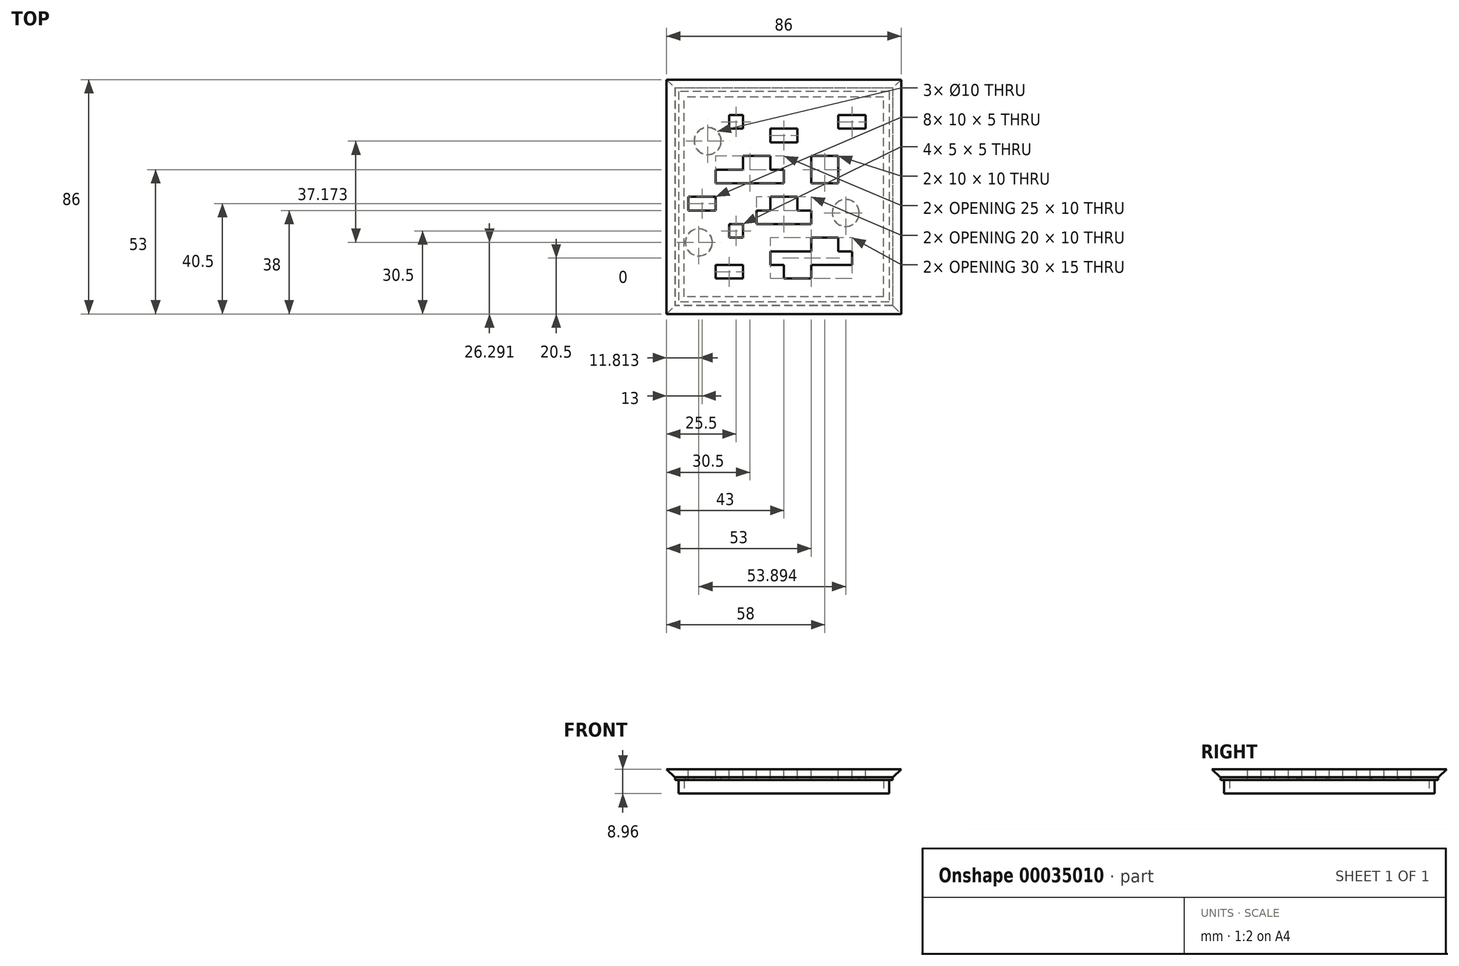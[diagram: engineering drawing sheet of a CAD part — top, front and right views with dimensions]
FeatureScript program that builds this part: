
annotation { "Feature Type Name" : "Feature", "Feature Type Description" : "" }
export const myFeature = defineFeature(function(context is Context, id is Id, definition is map)
    precondition{}
    {
        {
            var Q0;
            Q0=qCreatedBy(makeId("Top.planeOp"),FACE);
            var sketch = newSketch(context, id + "F0", { "sketchPlane" : qUnion([Q0])});
            skLineSegment(sketch, "E0.bottom", {"start": v(38.73, 38.72) * mm, "end": v(-38.72, 38.73) * mm});
            skLineSegment(sketch, "E0.top", {"start": v(38.72, -38.73) * mm, "end": v(-38.73, -38.72) * mm});
            skLineSegment(sketch, "E0.left", {"start": v(38.73, 38.72) * mm, "end": v(38.72, -38.73) * mm});
            skLineSegment(sketch, "E0.right", {"start": v(-38.72, 38.73) * mm, "end": v(-38.73, -38.72) * mm});
            skPoint(sketch, "E0.middle", {"position": v(0, 0) * mm});
            skLineSegment(sketch, "E1.0", {"start": v(38.62, 38.62) * mm, "end": v(-38.62, 38.62) * mm});
            skLineSegment(sketch, "E1.1", {"start": v(38.62, 38.62) * mm, "end": v(38.62, -38.63) * mm});
            skLineSegment(sketch, "E1.2", {"start": v(38.62, -38.63) * mm, "end": v(-38.62, -38.62) * mm});
            skLineSegment(sketch, "E1.3", {"start": v(-38.62, 38.62) * mm, "end": v(-38.62, -38.62) * mm});
            skLineSegment(sketch, "E2.bottom", {"start": v(36.62, -36.62) * mm, "end": v(-36.62, -36.62) * mm});
            skLineSegment(sketch, "E2.top", {"start": v(36.62, 36.62) * mm, "end": v(-36.62, 36.62) * mm});
            skLineSegment(sketch, "E2.left", {"start": v(36.62, -36.62) * mm, "end": v(36.62, 36.62) * mm});
            skLineSegment(sketch, "E2.right", {"start": v(-36.62, -36.62) * mm, "end": v(-36.62, 36.62) * mm});
            skSolve(sketch);
        }
        {
            var Q0;
            Q0=makeQuery(id+"F0.imprint","IMPRINT",FACE,{"disambiguationData":[TD([[makeQuery(id+"F0.imprint","IMPRINT",EDGE,{"derivedFrom":sQuery(id+"F0.wireOp",EDGE,"E1.0")}),1.0]])]});
            extrude(context, id + "F1", {"entities" : qUnion([Q0]), "depth" : 5 * mm});
        }
        {
            var Q0;
            Q0=makeQuery(id+"F1.opExtrude","CAP_FACE",FACE,{"disambiguationData":[OSD([sQuery(id+"F0.wireOp",EDGE,"E1.0"),sQuery(id+"F0.wireOp",EDGE,"E1.1"),sQuery(id+"F0.wireOp",EDGE,"E1.2"),sQuery(id+"F0.wireOp",EDGE,"E1.3")])],"isStart":false});
            var sketch = newSketch(context, id + "F2", { "sketchPlane" : qUnion([Q0])});
            skLineSegment(sketch, "E3.bottom", {"start": v(40, 40) * mm, "end": v(-40, 40) * mm});
            skLineSegment(sketch, "E3.top", {"start": v(40, -40) * mm, "end": v(-40, -40) * mm});
            skLineSegment(sketch, "E3.left", {"start": v(40, 40) * mm, "end": v(40, -40) * mm});
            skLineSegment(sketch, "E3.right", {"start": v(-40, 40) * mm, "end": v(-40, -40) * mm});
            skPoint(sketch, "E3.middle", {"position": v(0, 0) * mm});
            skLineSegment(sketch, "E4.0", {"start": v(39.9, 39.9) * mm, "end": v(39.9, -39.9) * mm});
            skLineSegment(sketch, "E4.1", {"start": v(39.9, 39.9) * mm, "end": v(-39.9, 39.9) * mm});
            skLineSegment(sketch, "E4.2", {"start": v(-39.9, 39.9) * mm, "end": v(-39.9, -39.9) * mm});
            skLineSegment(sketch, "E4.3", {"start": v(39.9, -39.9) * mm, "end": v(-39.9, -39.9) * mm});
            skSolve(sketch);
        }
        {
            var Q0;
            Q0=makeQuery(id+"F2.imprint","IMPRINT",FACE,{"disambiguationData":[TD([[makeQuery(id+"F2.imprint","IMPRINT",EDGE,{"derivedFrom":sQuery(id+"F2.wireOp",EDGE,"E4.0")}),-1.0]])]});
            var Q1;
            Q1=makeQuery(id+"F2.imprint","IMPRINT",FACE,{"disambiguationData":[TD([[makeQuery(id+"F2.imprint","IMPRINT",EDGE,{"derivedFrom":makeQuery(id+"F1.opExtrude","CAP_EDGE",EDGE,{"disambiguationData":[OSD([sQuery(id+"F0.wireOp",EDGE,"E1.0")])],"isStart":false})}),1.0]])]});
            var Q2;
            Q2=makeQuery(id+"F2.imprint","IMPRINT",FACE,{"disambiguationData":[TD([[makeQuery(id+"F2.imprint","IMPRINT",EDGE,{"derivedFrom":makeQuery(id+"F1.opExtrude","CAP_EDGE",EDGE,{"disambiguationData":[OSD([sQuery(id+"F0.wireOp",EDGE,"E2.bottom")])],"isStart":false})}),-1.0]])]});
            extrude(context, id + "F3", {"entities" : qUnion([Q0, Q1, Q2]), "operationType" : NewBodyOperationType.ADD, "depth" : 0.96 * mm});
        }
        {
            var Q0;
            Q0=makeQuery(id+"F3.opExtrude","CAP_FACE",FACE,{"disambiguationData":[OSD([sQuery(id+"F2.wireOp",EDGE,"E4.0"),sQuery(id+"F2.wireOp",EDGE,"E4.1"),sQuery(id+"F2.wireOp",EDGE,"E4.2"),sQuery(id+"F2.wireOp",EDGE,"E4.3")])],"isStart":false});
            var sketch = newSketch(context, id + "F4", { "sketchPlane" : qUnion([Q0])});
            skLineSegment(sketch, "E5.bottom", {"start": v(-34.9, -34.9) * mm, "end": v(34.9, -34.9) * mm, "construction": true});
            skLineSegment(sketch, "E5.top", {"start": v(-34.9, 34.9) * mm, "end": v(34.9, 34.9) * mm, "construction": true});
            skLineSegment(sketch, "E5.left", {"start": v(-34.9, -34.9) * mm, "end": v(-34.9, 34.9) * mm, "construction": true});
            skLineSegment(sketch, "E5.right", {"start": v(34.9, -34.9) * mm, "end": v(34.9, 34.9) * mm, "construction": true});
            skPoint(sketch, "E5.middle", {"position": v(0, 0) * mm});
            skCircle(sketch, "E6", {"center": v(-31.19, -16.7) * mm, "radius": 5 * mm});
            skCircle(sketch, "E7", {"center": v(22.7, -5.92) * mm, "radius": 5 * mm});
            skCircle(sketch, "E8", {"center": v(-27.93, 20.46) * mm, "radius": 5 * mm});
            skSolve(sketch);
        }
        {
            var Q0;
            Q0=makeQuery(id+"F4.imprint","IMPRINT",FACE,{"disambiguationData":[TD([[makeQuery(id+"F4.imprint","IMPRINT",EDGE,{"derivedFrom":sQuery(id+"F4.wireOp",EDGE,"E6")}),1.0]])]});
            var Q1;
            Q1=makeQuery(id+"F4.imprint","IMPRINT",FACE,{"disambiguationData":[TD([[makeQuery(id+"F4.imprint","IMPRINT",EDGE,{"derivedFrom":sQuery(id+"F4.wireOp",EDGE,"E8")}),1.0]])]});
            var Q2;
            Q2=makeQuery(id+"F4.imprint","IMPRINT",FACE,{"disambiguationData":[TD([[makeQuery(id+"F4.imprint","IMPRINT",EDGE,{"derivedFrom":sQuery(id+"F4.wireOp",EDGE,"E7")}),1.0]])]});
            var Q3;
            Q3=makeQuery(id+"F1.opExtrude","CAP_FACE",FACE,{"disambiguationData":[OSD([sQuery(id+"F0.wireOp",EDGE,"E1.0"),sQuery(id+"F0.wireOp",EDGE,"E1.1"),sQuery(id+"F0.wireOp",EDGE,"E1.2"),sQuery(id+"F0.wireOp",EDGE,"E1.3"),sQuery(id+"F0.wireOp",EDGE,"E2.bottom"),sQuery(id+"F0.wireOp",EDGE,"E2.top"),sQuery(id+"F0.wireOp",EDGE,"E2.left"),sQuery(id+"F0.wireOp",EDGE,"E2.right")])],"isStart":true});
            extrude(context, id + "F5", {"entities" : qUnion([Q0, Q1, Q2]), "operationType" : NewBodyOperationType.REMOVE, "endBound" : BoundingType.UP_TO_SURFACE, "oppositeDirection" : true, "endBoundEntityFace" : qUnion([Q3]), "depth" : 25 * mm});
        }
        {
            var Q0;
            Q0=makeQuery(id+"F3.opExtrude","CAP_FACE",FACE,{"disambiguationData":[OSD([sQuery(id+"F2.wireOp",EDGE,"E4.0"),sQuery(id+"F2.wireOp",EDGE,"E4.1"),sQuery(id+"F2.wireOp",EDGE,"E4.2"),sQuery(id+"F2.wireOp",EDGE,"E4.3")])],"isStart":false});
            var sketch = newSketch(context, id + "F6", { "sketchPlane" : qUnion([Q0])});
            skLineSegment(sketch, "E9.bottom", {"start": v(43, 43) * mm, "end": v(-43, 43) * mm});
            skLineSegment(sketch, "E9.top", {"start": v(43, -43) * mm, "end": v(-43, -43) * mm});
            skLineSegment(sketch, "E9.left", {"start": v(43, 43) * mm, "end": v(43, -43) * mm});
            skLineSegment(sketch, "E9.right", {"start": v(-43, 43) * mm, "end": v(-43, -43) * mm});
            skPoint(sketch, "E9.middle", {"position": v(0, 0) * mm});
            skSolve(sketch);
        }
        {
            var Q0;
            Q0 = qSketchRegion(id + "F6", true);
            extrude(context, id + "F7", {"entities" : qUnion([Q0]), "depth" : 3 * mm});
        }
        {
            var Q0;
            Q0=makeQuery(id+"F4.imprint","IMPRINT",FACE,{"disambiguationData":[TD([[makeQuery(id+"F4.imprint","IMPRINT",EDGE,{"derivedFrom":sQuery(id+"F4.wireOp",EDGE,"E6")}),-1.0]])]});
            var sketch = newSketch(context, id + "F8", { "sketchPlane" : qUnion([Q0])});
            skPoint(sketch, "E10.0", {"position": v(-31.19, -16.7) * mm});
            skCircle(sketch, "E11", {"center": v(-31.19, -16.7) * mm, "radius": 4.9 * mm});
            skPoint(sketch, "E12.0", {"position": v(22.7, -5.92) * mm});
            skPoint(sketch, "E13.0", {"position": v(-27.93, 20.46) * mm});
            skCircle(sketch, "E14", {"center": v(-27.93, 20.46) * mm, "radius": 4.9 * mm});
            skCircle(sketch, "E15", {"center": v(22.7, -5.92) * mm, "radius": 4.9 * mm});
            skSolve(sketch);
        }
        {
            var Q0;
            Q0=makeQuery(id+"F8.imprint","IMPRINT",FACE,{"disambiguationData":[TD([[makeQuery(id+"F8.imprint","IMPRINT",EDGE,{"derivedFrom":sQuery(id+"F8.wireOp",EDGE,"E11")}),1.0]])]});
            var Q1;
            Q1=makeQuery(id+"F8.imprint","IMPRINT",FACE,{"disambiguationData":[TD([[makeQuery(id+"F8.imprint","IMPRINT",EDGE,{"derivedFrom":sQuery(id+"F8.wireOp",EDGE,"E15")}),1.0]])]});
            var Q2;
            Q2=makeQuery(id+"F8.imprint","IMPRINT",FACE,{"disambiguationData":[TD([[makeQuery(id+"F8.imprint","IMPRINT",EDGE,{"derivedFrom":sQuery(id+"F8.wireOp",EDGE,"E14")}),1.0]])]});
            extrude(context, id + "F9", {"entities" : qUnion([Q0, Q1, Q2]), "operationType" : NewBodyOperationType.ADD, "oppositeDirection" : true, "depth" : 1 * mm});
        }
        {
            var Q0;
            Q0=makeQuery(id+"F7.opExtrude","CAP_FACE",FACE,{"disambiguationData":[OSD([sQuery(id+"F6.wireOp",EDGE,"E9.bottom"),sQuery(id+"F6.wireOp",EDGE,"E9.top"),sQuery(id+"F6.wireOp",EDGE,"E9.left"),sQuery(id+"F6.wireOp",EDGE,"E9.right")])],"isStart":false});
            var sketch = newSketch(context, id + "F10", { "sketchPlane" : qUnion([Q0])});
            skLineSegment(sketch, "E16.bottom", {"start": v(40, -40) * mm, "end": v(-40, -40) * mm, "construction": true});
            skLineSegment(sketch, "E16.top", {"start": v(40, 40) * mm, "end": v(-40, 40) * mm, "construction": true});
            skLineSegment(sketch, "E16.left", {"start": v(40, -40) * mm, "end": v(40, 40) * mm, "construction": true});
            skLineSegment(sketch, "E16.right", {"start": v(-40, -40) * mm, "end": v(-40, 40) * mm, "construction": true});
            skPoint(sketch, "E16.middle", {"position": v(0, 0) * mm});
            skLineSegment(sketch, "E17", {"start": v(-35, 40) * mm, "end": v(-35, -40) * mm, "construction": true});
            skLineSegment(sketch, "E18.1.0.0", {"start": v(-30, 40) * mm, "end": v(-30, -40) * mm, "construction": true});
            skLineSegment(sketch, "E18.2.0.0", {"start": v(-25, 40) * mm, "end": v(-25, -40) * mm, "construction": true});
            skLineSegment(sketch, "E18.3.0.0", {"start": v(-20, 40) * mm, "end": v(-20, -40) * mm, "construction": true});
            skLineSegment(sketch, "E18.4.0.0", {"start": v(-15, 40) * mm, "end": v(-15, -40) * mm, "construction": true});
            skLineSegment(sketch, "E18.5.0.0", {"start": v(-10, 40) * mm, "end": v(-10, -40) * mm, "construction": true});
            skLineSegment(sketch, "E18.6.0.0", {"start": v(-5, 40) * mm, "end": v(-5, -40) * mm, "construction": true});
            skLineSegment(sketch, "E18.7.0.0", {"start": v(0, 40) * mm, "end": v(0, -40) * mm, "construction": true});
            skLineSegment(sketch, "E18.8.0.0", {"start": v(5, 40) * mm, "end": v(5, -40) * mm, "construction": true});
            skLineSegment(sketch, "E18.9.0.0", {"start": v(10, 40) * mm, "end": v(10, -40) * mm, "construction": true});
            skLineSegment(sketch, "E18.10.0.0", {"start": v(15, 40) * mm, "end": v(15, -40) * mm, "construction": true});
            skLineSegment(sketch, "E18.11.0.0", {"start": v(20, 40) * mm, "end": v(20, -40) * mm, "construction": true});
            skLineSegment(sketch, "E18.12.0.0", {"start": v(25, 40) * mm, "end": v(25, -40) * mm, "construction": true});
            skLineSegment(sketch, "E18.13.0.0", {"start": v(30, 40) * mm, "end": v(30, -40) * mm, "construction": true});
            skLineSegment(sketch, "E18.14.0.0", {"start": v(35, 40) * mm, "end": v(35, -40) * mm, "construction": true});
            skLineSegment(sketch, "E18.direction1", {"start": v(-35, -40) * mm, "end": v(-30, -40) * mm, "construction": true});
            skLineSegment(sketch, "E19", {"start": v(-40, 35) * mm, "end": v(40, 35) * mm, "construction": true});
            skLineSegment(sketch, "E20.0.1.0", {"start": v(-40, 30) * mm, "end": v(40, 30) * mm, "construction": true});
            skLineSegment(sketch, "E20.0.2.0", {"start": v(-40, 25) * mm, "end": v(40, 25) * mm, "construction": true});
            skLineSegment(sketch, "E20.0.3.0", {"start": v(-40, 20) * mm, "end": v(40, 20) * mm, "construction": true});
            skLineSegment(sketch, "E20.0.4.0", {"start": v(-40, 15) * mm, "end": v(40, 15) * mm, "construction": true});
            skLineSegment(sketch, "E20.0.5.0", {"start": v(-40, 10) * mm, "end": v(40, 10) * mm, "construction": true});
            skLineSegment(sketch, "E20.0.6.0", {"start": v(-40, 5) * mm, "end": v(40, 5) * mm, "construction": true});
            skLineSegment(sketch, "E20.0.7.0", {"start": v(-40, 0) * mm, "end": v(40, 0) * mm, "construction": true});
            skLineSegment(sketch, "E20.0.8.0", {"start": v(-40, -5) * mm, "end": v(40, -5) * mm, "construction": true});
            skLineSegment(sketch, "E20.0.9.0", {"start": v(-40, -10) * mm, "end": v(40, -10) * mm, "construction": true});
            skLineSegment(sketch, "E20.0.10.0", {"start": v(-40, -15) * mm, "end": v(40, -15) * mm, "construction": true});
            skLineSegment(sketch, "E20.0.11.0", {"start": v(-40, -20) * mm, "end": v(40, -20) * mm, "construction": true});
            skLineSegment(sketch, "E20.0.12.0", {"start": v(-40, -25) * mm, "end": v(40, -25) * mm, "construction": true});
            skLineSegment(sketch, "E20.0.13.0", {"start": v(-40, -30) * mm, "end": v(40, -30) * mm, "construction": true});
            skLineSegment(sketch, "E20.0.14.0", {"start": v(-40, -35) * mm, "end": v(40, -35) * mm, "construction": true});
            skLineSegment(sketch, "E20.direction1", {"start": v(-40, 35) * mm, "end": v(-15, 35) * mm, "construction": true});
            skLineSegment(sketch, "E20.direction2", {"start": v(-40, 35) * mm, "end": v(-40, 30) * mm, "construction": true});
            skLineSegment(sketch, "E21.bottom", {"start": v(-20, 30) * mm, "end": v(-15, 30) * mm});
            skLineSegment(sketch, "E21.top", {"start": v(-20, 25) * mm, "end": v(-15, 25) * mm});
            skLineSegment(sketch, "E21.left", {"start": v(-20, 30) * mm, "end": v(-20, 25) * mm});
            skLineSegment(sketch, "E21.right", {"start": v(-15, 30) * mm, "end": v(-15, 25) * mm});
            skLineSegment(sketch, "E22.bottom", {"start": v(-5, 25) * mm, "end": v(5, 25) * mm});
            skLineSegment(sketch, "E22.top", {"start": v(-5, 20) * mm, "end": v(5, 20) * mm});
            skLineSegment(sketch, "E22.left", {"start": v(-5, 25) * mm, "end": v(-5, 20) * mm});
            skLineSegment(sketch, "E22.right", {"start": v(5, 25) * mm, "end": v(5, 20) * mm});
            skLineSegment(sketch, "E23.bottom", {"start": v(20, 25) * mm, "end": v(30, 25) * mm});
            skLineSegment(sketch, "E23.top", {"start": v(20, 30) * mm, "end": v(30, 30) * mm});
            skLineSegment(sketch, "E23.left", {"start": v(20, 25) * mm, "end": v(20, 30) * mm});
            skLineSegment(sketch, "E23.right", {"start": v(30, 25) * mm, "end": v(30, 30) * mm});
            skLineSegment(sketch, "E24.bottom", {"start": v(20, 15) * mm, "end": v(10, 15) * mm});
            skLineSegment(sketch, "E24.top", {"start": v(20, 5) * mm, "end": v(10, 5) * mm});
            skLineSegment(sketch, "E24.left", {"start": v(20, 15) * mm, "end": v(20, 5) * mm});
            skLineSegment(sketch, "E24.right", {"start": v(10, 15) * mm, "end": v(10, 5) * mm});
            skLineSegment(sketch, "E25", {"start": v(0, 5) * mm, "end": v(0, 10) * mm});
            skLineSegment(sketch, "E26", {"start": v(-5, 10) * mm, "end": v(-5, 15) * mm});
            skLineSegment(sketch, "E27", {"start": v(-5, 15) * mm, "end": v(-15, 15) * mm});
            skLineSegment(sketch, "E28", {"start": v(-15, 15) * mm, "end": v(-15, 10) * mm});
            skLineSegment(sketch, "E29", {"start": v(-15, 10) * mm, "end": v(-25, 10) * mm});
            skLineSegment(sketch, "E30", {"start": v(-25, 10) * mm, "end": v(-25, 5) * mm});
            skLineSegment(sketch, "E31", {"start": v(-25, 5) * mm, "end": v(0, 5) * mm});
            skLineSegment(sketch, "E32.bottom", {"start": v(-25, 0) * mm, "end": v(-35, 0) * mm});
            skLineSegment(sketch, "E32.top", {"start": v(-25, -5) * mm, "end": v(-35, -5) * mm});
            skLineSegment(sketch, "E32.left", {"start": v(-25, 0) * mm, "end": v(-25, -5) * mm});
            skLineSegment(sketch, "E32.right", {"start": v(-35, 0) * mm, "end": v(-35, -5) * mm});
            skLineSegment(sketch, "E33.bottom", {"start": v(-20, -10) * mm, "end": v(-15, -10) * mm});
            skLineSegment(sketch, "E33.top", {"start": v(-20, -15) * mm, "end": v(-15, -15) * mm});
            skLineSegment(sketch, "E33.left", {"start": v(-20, -10) * mm, "end": v(-20, -15) * mm});
            skLineSegment(sketch, "E33.right", {"start": v(-15, -10) * mm, "end": v(-15, -15) * mm});
            skLineSegment(sketch, "E34.bottom", {"start": v(-15, -25) * mm, "end": v(-25, -25) * mm});
            skLineSegment(sketch, "E34.top", {"start": v(-15, -30) * mm, "end": v(-25, -30) * mm});
            skLineSegment(sketch, "E34.left", {"start": v(-15, -25) * mm, "end": v(-15, -30) * mm});
            skLineSegment(sketch, "E34.right", {"start": v(-25, -25) * mm, "end": v(-25, -30) * mm});
            skLineSegment(sketch, "E35", {"start": v(5, 0) * mm, "end": v(-5, 0) * mm});
            skLineSegment(sketch, "E36", {"start": v(-5, 0) * mm, "end": v(-5, -5) * mm});
            skLineSegment(sketch, "E37", {"start": v(-5, -5) * mm, "end": v(-10, -5) * mm});
            skLineSegment(sketch, "E38", {"start": v(-10, -5) * mm, "end": v(-10, -10) * mm});
            skLineSegment(sketch, "E39", {"start": v(-10, -10) * mm, "end": v(10, -10) * mm});
            skLineSegment(sketch, "E40", {"start": v(10, -10) * mm, "end": v(10, -5) * mm});
            skLineSegment(sketch, "E41", {"start": v(10, -5) * mm, "end": v(5, -5) * mm});
            skLineSegment(sketch, "E42", {"start": v(5, -5) * mm, "end": v(5, 0) * mm});
            skLineSegment(sketch, "E43", {"start": v(10, -15) * mm, "end": v(20, -15) * mm});
            skLineSegment(sketch, "E44", {"start": v(20, -15) * mm, "end": v(20, -20) * mm});
            skLineSegment(sketch, "E45", {"start": v(20, -20) * mm, "end": v(25, -20) * mm});
            skLineSegment(sketch, "E46", {"start": v(25, -20) * mm, "end": v(25, -25) * mm});
            skLineSegment(sketch, "E47", {"start": v(25, -25) * mm, "end": v(10, -25) * mm});
            skLineSegment(sketch, "E48", {"start": v(10, -25) * mm, "end": v(10, -30) * mm});
            skLineSegment(sketch, "E49", {"start": v(10, -30) * mm, "end": v(0, -30) * mm});
            skLineSegment(sketch, "E50", {"start": v(0, -30) * mm, "end": v(0, -25) * mm});
            skLineSegment(sketch, "E51", {"start": v(0, -25) * mm, "end": v(-5, -25) * mm});
            skLineSegment(sketch, "E52", {"start": v(-5, -25) * mm, "end": v(-5, -20) * mm});
            skLineSegment(sketch, "E53", {"start": v(-5, -20) * mm, "end": v(10, -20) * mm});
            skLineSegment(sketch, "E54", {"start": v(10, -20) * mm, "end": v(10, -15) * mm});
            skLineSegment(sketch, "E55", {"start": v(0, 10) * mm, "end": v(-5, 10) * mm});
            skSolve(sketch);
        }
        {
            var Q0;
            Q0=makeQuery(id+"F10.imprint","IMPRINT",FACE,{"disambiguationData":[TD([[makeQuery(id+"F10.imprint","IMPRINT",EDGE,{"derivedFrom":sQuery(id+"F10.wireOp",EDGE,"E34.bottom")}),1.0]])]});
            var Q1;
            Q1=makeQuery(id+"F10.imprint","IMPRINT",FACE,{"disambiguationData":[TD([[makeQuery(id+"F10.imprint","IMPRINT",EDGE,{"derivedFrom":sQuery(id+"F10.wireOp",EDGE,"E43")}),-1.0]])]});
            var Q2;
            Q2=makeQuery(id+"F10.imprint","IMPRINT",FACE,{"disambiguationData":[TD([[makeQuery(id+"F10.imprint","IMPRINT",EDGE,{"derivedFrom":sQuery(id+"F10.wireOp",EDGE,"E35")}),1.0]])]});
            var Q3;
            Q3=makeQuery(id+"F10.imprint","IMPRINT",FACE,{"disambiguationData":[TD([[makeQuery(id+"F10.imprint","IMPRINT",EDGE,{"derivedFrom":sQuery(id+"F10.wireOp",EDGE,"E33.bottom")}),-1.0]])]});
            var Q4;
            Q4=makeQuery(id+"F10.imprint","IMPRINT",FACE,{"disambiguationData":[TD([[makeQuery(id+"F10.imprint","IMPRINT",EDGE,{"derivedFrom":sQuery(id+"F10.wireOp",EDGE,"E32.bottom")}),1.0]])]});
            var Q5;
            Q5=makeQuery(id+"F10.imprint","IMPRINT",FACE,{"disambiguationData":[TD([[makeQuery(id+"F10.imprint","IMPRINT",EDGE,{"derivedFrom":sQuery(id+"F10.wireOp",EDGE,"E21.bottom")}),-1.0]])]});
            var Q6;
            Q6=makeQuery(id+"F10.imprint","IMPRINT",FACE,{"disambiguationData":[TD([[makeQuery(id+"F10.imprint","IMPRINT",EDGE,{"derivedFrom":sQuery(id+"F10.wireOp",EDGE,"E22.bottom")}),-1.0]])]});
            var Q7;
            Q7=makeQuery(id+"F10.imprint","IMPRINT",FACE,{"disambiguationData":[TD([[makeQuery(id+"F10.imprint","IMPRINT",EDGE,{"derivedFrom":sQuery(id+"F10.wireOp",EDGE,"E24.bottom")}),1.0]])]});
            var Q8;
            Q8=makeQuery(id+"F10.imprint","IMPRINT",FACE,{"disambiguationData":[TD([[makeQuery(id+"F10.imprint","IMPRINT",EDGE,{"derivedFrom":sQuery(id+"F10.wireOp",EDGE,"E23.bottom")}),1.0]])]});
            var Q9;
            Q9=makeQuery(id+"F10.imprint","IMPRINT",FACE,{"disambiguationData":[TD([[makeQuery(id+"F10.imprint","IMPRINT",EDGE,{"derivedFrom":sQuery(id+"F10.wireOp",EDGE,"E25")}),1.0]])]});
            extrude(context, id + "F11", {"entities" : qUnion([Q0, Q1, Q2, Q3, Q4, Q5, Q6, Q7, Q8, Q9]), "operationType" : NewBodyOperationType.REMOVE, "oppositeDirection" : true, "depth" : 25 * mm});
        }
        {
            var Q0;
            Q0=makeQuery(id+"F7.opExtrude","SWEPT_FACE",FACE,{"disambiguationData":[OSD([sQuery(id+"F6.wireOp",EDGE,"E9.top")])]});
            cPlane(context, id + "F12", {"entities" : qUnion([Q0]), "cplaneType" : CPlaneType.OFFSET, "offset" : 0 * mm, "width" : 150 * mm, "height" : 150 * mm});
        }
        {
            var Q0;
            Q0=makeQuery(id+"F7.opExtrude","SWEPT_FACE",FACE,{"disambiguationData":[OSD([sQuery(id+"F6.wireOp",EDGE,"E9.right")])]});
            cPlane(context, id + "F13", {"entities" : qUnion([Q0]), "cplaneType" : CPlaneType.OFFSET, "offset" : 0 * mm, "width" : 150 * mm, "height" : 150 * mm});
        }
        {
            var Q0;
            Q0=makeQuery(id+"F7.opExtrude","SWEPT_FACE",FACE,{"disambiguationData":[OSD([sQuery(id+"F6.wireOp",EDGE,"E9.bottom")])]});
            cPlane(context, id + "F14", {"entities" : qUnion([Q0]), "cplaneType" : CPlaneType.OFFSET, "offset" : 0 * mm, "width" : 150 * mm, "height" : 150 * mm});
        }
        {
            var Q0;
            Q0=makeQuery(id+"F7.opExtrude","SWEPT_FACE",FACE,{"disambiguationData":[OSD([sQuery(id+"F6.wireOp",EDGE,"E9.left")])]});
            cPlane(context, id + "F15", {"entities" : qUnion([Q0]), "cplaneType" : CPlaneType.OFFSET, "offset" : 0 * mm, "width" : 150 * mm, "height" : 150 * mm});
        }
        {
            var Q0;
            Q0=qCreatedBy(id+"F12.planeOp",FACE);
            var sketch = newSketch(context, id + "F16", { "sketchPlane" : qUnion([Q0])});
            skLineSegment(sketch, "E56", {"start": v(-43, 5.96) * mm, "end": v(-43, 8.96) * mm});
            skLineSegment(sketch, "E57", {"start": v(-43, 8.96) * mm, "end": v(-40, 5.96) * mm});
            skLineSegment(sketch, "E58", {"start": v(-40, 5.96) * mm, "end": v(-43, 5.96) * mm});
            skSolve(sketch);
        }
        {
            var Q0;
            Q0=qCreatedBy(id+"F13.planeOp",FACE);
            var sketch = newSketch(context, id + "F17", { "sketchPlane" : qUnion([Q0])});
            skLineSegment(sketch, "E59", {"start": v(43, 8.96) * mm, "end": v(40, 5.96) * mm});
            skLineSegment(sketch, "E60", {"start": v(40, 5.96) * mm, "end": v(43, 5.96) * mm});
            skLineSegment(sketch, "E61", {"start": v(43, 8.96) * mm, "end": v(43, 5.96) * mm});
            skSolve(sketch);
        }
        {
            var Q0;
            Q0=qCreatedBy(id+"F14.planeOp",FACE);
            var sketch = newSketch(context, id + "F18", { "sketchPlane" : qUnion([Q0])});
            skLineSegment(sketch, "E62", {"start": v(-43, 8.96) * mm, "end": v(-40, 5.96) * mm});
            skLineSegment(sketch, "E63", {"start": v(-40, 5.96) * mm, "end": v(-43, 5.96) * mm});
            skLineSegment(sketch, "E64", {"start": v(-43, 5.96) * mm, "end": v(-43, 8.96) * mm});
            skSolve(sketch);
        }
        {
            var Q0;
            Q0=qCreatedBy(id+"F15.planeOp",FACE);
            var sketch = newSketch(context, id + "F19", { "sketchPlane" : qUnion([Q0])});
            skLineSegment(sketch, "E65", {"start": v(43, 8.96) * mm, "end": v(40, 5.96) * mm});
            skLineSegment(sketch, "E66", {"start": v(40, 5.96) * mm, "end": v(43, 5.96) * mm});
            skLineSegment(sketch, "E67", {"start": v(43, 5.96) * mm, "end": v(43, 8.96) * mm});
            skSolve(sketch);
        }
        {
            var Q0;
            Q0=makeQuery(id+"F16.imprint","IMPRINT",FACE,{"disambiguationData":[TD([[makeQuery(id+"F16.imprint","IMPRINT",EDGE,{"derivedFrom":sQuery(id+"F16.wireOp",EDGE,"E56")}),-1.0]])]});
            extrude(context, id + "F20", {"entities" : qUnion([Q0]), "operationType" : NewBodyOperationType.REMOVE, "endBound" : BoundingType.UP_TO_NEXT, "oppositeDirection" : true, "depth" : 25 * mm});
        }
        {
            var Q0;
            Q0=makeQuery(id+"F17.imprint","IMPRINT",FACE,{"disambiguationData":[TD([[makeQuery(id+"F17.imprint","IMPRINT",EDGE,{"derivedFrom":sQuery(id+"F17.wireOp",EDGE,"E59")}),1.0]])]});
            var Q1;
            Q1=makeQuery(id+"F7.opExtrude","SWEPT_FACE",FACE,{"disambiguationData":[OSD([sQuery(id+"F6.wireOp",EDGE,"E9.left")])]});
            extrude(context, id + "F21", {"entities" : qUnion([Q0]), "operationType" : NewBodyOperationType.REMOVE, "endBound" : BoundingType.UP_TO_SURFACE, "oppositeDirection" : true, "endBoundEntityFace" : qUnion([Q1]), "depth" : 25 * mm});
        }
        {
            var Q0;
            Q0=makeQuery(id+"F18.imprint","IMPRINT",FACE,{"disambiguationData":[TD([[makeQuery(id+"F18.imprint","IMPRINT",EDGE,{"derivedFrom":sQuery(id+"F18.wireOp",EDGE,"E62")}),-1.0]])]});
            extrude(context, id + "F22", {"entities" : qUnion([Q0]), "operationType" : NewBodyOperationType.REMOVE, "endBound" : BoundingType.UP_TO_NEXT, "oppositeDirection" : true, "depth" : 25 * mm});
        }
        {
            var Q0;
            Q0=makeQuery(id+"F19.imprint","IMPRINT",FACE,{"disambiguationData":[TD([[makeQuery(id+"F19.imprint","IMPRINT",EDGE,{"derivedFrom":sQuery(id+"F19.wireOp",EDGE,"E65")}),1.0]])]});
            var Q1;
            Q1=makeQuery(id+"F20.boolean.opBoolean","COPY",FACE,{"derivedFrom":makeQuery(id+"F20.opExtrude","SWEPT_FACE",FACE,{"disambiguationData":[OSD([sQuery(id+"F16.wireOp",EDGE,"E57")])]})});
            extrude(context, id + "F23", {"entities" : qUnion([Q0]), "operationType" : NewBodyOperationType.REMOVE, "endBound" : BoundingType.UP_TO_SURFACE, "oppositeDirection" : true, "endBoundEntityFace" : qUnion([Q1]), "depth" : 25 * mm});
        }
    });
